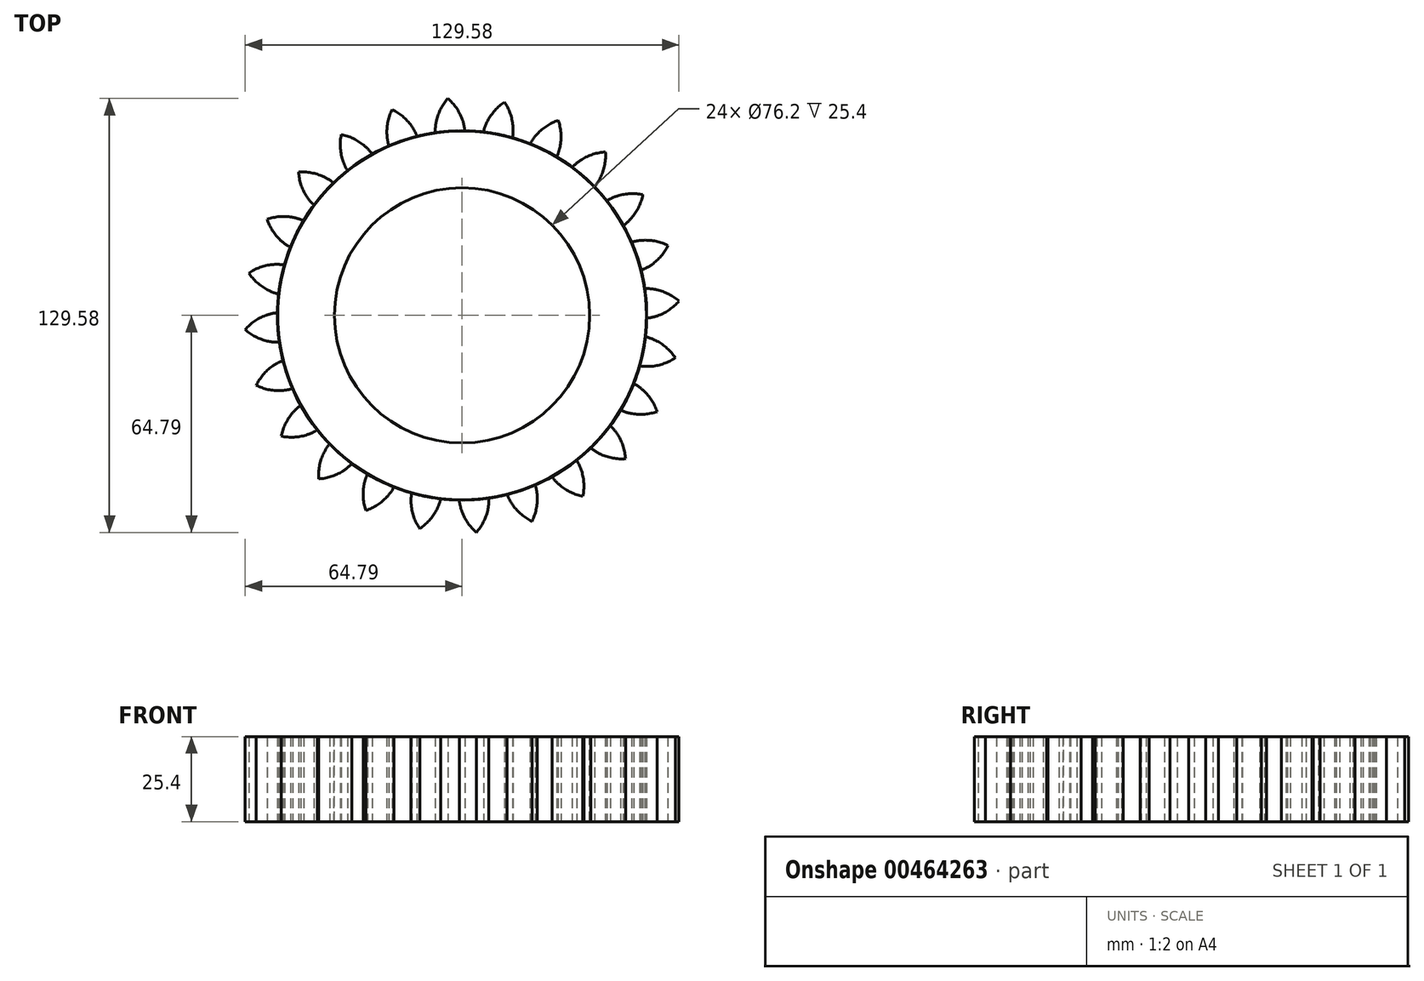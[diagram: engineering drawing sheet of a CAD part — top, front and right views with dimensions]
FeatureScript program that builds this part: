
annotation { "Feature Type Name" : "Feature", "Feature Type Description" : "" }
export const myFeature = defineFeature(function(context is Context, id is Id, definition is map)
    precondition{}
    {
        {
            var Q0;
            Q0=qCreatedBy(makeId("Top.planeOp"),FACE);
            var sketch = newSketch(context, id + "F0", { "sketchPlane" : qUnion([Q0])});
            skCircle(sketch, "E0", {"center": v(0, 0) * mm, "radius": 63.5 * mm, "construction": true});
            skCircle(sketch, "E1", {"center": v(0, 0) * mm, "radius": 58.67 * mm, "construction": true});
            skCircle(sketch, "E2", {"center": v(0, 0) * mm, "radius": 53.72 * mm});
            skLineSegment(sketch, "E3", {"start": v(0, 0) * mm, "end": v(0, 149.1) * mm, "construction": true});
            skLineSegment(sketch, "E4", {"start": v(0, 0) * mm, "end": v(-9.77, 149.1) * mm, "construction": true});
            skLineSegment(sketch, "E5", {"start": v(0, 58.67) * mm, "end": v(-102.58, 58.67) * mm, "construction": true});
            skLineSegment(sketch, "E6", {"start": v(0, 58.67) * mm, "end": v(-102.58, 21.34) * mm, "construction": true});
            skCircle(sketch, "E7", {"center": v(0, 0) * mm, "radius": 55.14 * mm});
            skCircle(sketch, "E8", {"center": v(0, 58.67) * mm, "radius": 14.6 * mm, "construction": true});
            skCircle(sketch, "E9", {"center": v(-13.72, 53.68) * mm, "radius": 14.6 * mm, "construction": true});
            skArc(sketch, "E10", {"start": v(0, 58.67) * mm, "mid": v(-1.74, 62) * mm, "end": v(-4.25, 64.8) * mm});
            skArc(sketch, "E11", {"start": v(0.88, 53.71) * mm, "mid": v(0.67, 56.23) * mm, "end": v(0, 58.67) * mm});
            skArc(sketch, "E12.MirrorCS", {"start": v(-7.66, 58.17) * mm, "mid": v(-6.37, 61.7) * mm, "end": v(-4.25, 64.8) * mm});
            skArc(sketch, "E13.MirrorCS", {"start": v(-7.88, 53.14) * mm, "mid": v(-8, 55.67) * mm, "end": v(-7.66, 58.17) * mm});
            skCircle(sketch, "E14", {"center": v(0, 0) * mm, "radius": 6.35 * mm});
            skSolve(sketch);
        }
        {
            var Q0;
            {var subQ0=sQuery(id+"F0.wireOp",EDGE,"E2");var subQ1=makeQuery(id+"F0.imprint","INTERSECT",VERTEX,{"derivedFrom":[subQ0,sQuery(id+"F0.wireOp",EDGE,"E11")]});Q0=makeQuery(id+"F0.imprint","IMPRINT",FACE,{"disambiguationData":[TD([[makeQuery(id+"F0.imprint","IMPRINT",EDGE,{"disambiguationData":[TD([[subQ1,-1.0]])],"derivedFrom":subQ0}),1.0]])]});}
            var Q1;
            {var subQ1=sQuery(id+"F0.wireOp",EDGE,"E10");Q1=makeQuery(id+"F0.imprint","IMPRINT",FACE,{"disambiguationData":[TD([[makeQuery(id+"F0.imprint","IMPRINT",EDGE,{"derivedFrom":subQ1}),1.0]])]});}
            var Q2;
            {var subQ0=sQuery(id+"F0.wireOp",EDGE,"E11");var subQ1=sQuery(id+"F0.wireOp",EDGE,"E2");var subQ2=makeQuery(id+"F0.imprint","INTERSECT",VERTEX,{"derivedFrom":[subQ1,subQ0]});Q2=makeQuery(id+"F0.imprint","IMPRINT",FACE,{"disambiguationData":[TD([[makeQuery(id+"F0.imprint","IMPRINT",EDGE,{"disambiguationData":[TD([[subQ2,-1.0]])],"derivedFrom":subQ1}),-1.0]])]});}
            var Q3;
            {var subQ0=sQuery(id+"F0.wireOp",EDGE,"E11");var subQ1=sQuery(id+"F0.wireOp",EDGE,"E2");var subQ2=makeQuery(id+"F0.imprint","INTERSECT",VERTEX,{"derivedFrom":[subQ1,subQ0]});Q3=makeQuery(id+"F0.imprint","IMPRINT",FACE,{"disambiguationData":[TD([[makeQuery(id+"F0.imprint","IMPRINT",EDGE,{"disambiguationData":[TD([[subQ2,1.0]])],"derivedFrom":subQ1}),-1.0]])]});}
            extrude(context, id + "F1", {"entities" : qUnion([Q0, Q1, Q2, Q3]), "depth" : 25.4 * mm});
        }
        {
            var Q0;
            Q0=makeQuery(id+"F1.opExtrude","SWEPT_BODY",BODY,{"disambiguationData":[OSD([sQuery(id+"F0.wireOp",EDGE,"E7"),sQuery(id+"F0.wireOp",EDGE,"E10"),sQuery(id+"F0.wireOp",EDGE,"E11"),sQuery(id+"F0.wireOp",EDGE,"E12.MirrorCS"),sQuery(id+"F0.wireOp",EDGE,"E13.MirrorCS")])]});
            var Q1;
            Q1=makeQuery(id+"F1.opExtrude","SWEPT_FACE",FACE,{"disambiguationData":[OSD([sQuery(id+"F0.wireOp",EDGE,"E7")])]});
            circularPattern(context, id + "F2", {"entities" : qUnion([Q0]), "axis" : qUnion([Q1]), "angle" : 360 * degree, "instanceCount" : 24, "equalSpace" : true});
        }
        {
            var Q0;
            Q0=makeQuery(id+"F1.opExtrude","CAP_FACE",FACE,{"disambiguationData":[OSD([sQuery(id+"F0.wireOp",EDGE,"E7"),sQuery(id+"F0.wireOp",EDGE,"E10"),sQuery(id+"F0.wireOp",EDGE,"E11"),sQuery(id+"F0.wireOp",EDGE,"E12.MirrorCS"),sQuery(id+"F0.wireOp",EDGE,"E13.MirrorCS")])],"isStart":false});
            var sketch = newSketch(context, id + "F3", { "sketchPlane" : qUnion([Q0])});
            skCircle(sketch, "E15", {"center": v(0, 0) * mm, "radius": 38.1 * mm});
            skSolve(sketch);
        }
        {
            var Q0;
            Q0=makeQuery(id+"F3.imprint","IMPRINT",FACE,{"disambiguationData":[TD([[makeQuery(id+"F3.imprint","IMPRINT",EDGE,{"derivedFrom":sQuery(id+"F3.wireOp",EDGE,"E15")}),1.0]])]});
            var Q1;
            Q1=sQuery(id+"F3.wireOp",EDGE,"E15");
            extrude(context, id + "F4", {"entities" : qUnion([Q0]), "operationType" : NewBodyOperationType.REMOVE, "surfaceEntities" : qUnion([Q1]), "oppositeDirection" : true, "depth" : 25.4 * mm});
        }
        {
            var Q0;
            Q0=makeQuery(id+"F2.opPattern","COPY",FACE,{"derivedFrom":makeQuery(id+"F1.opExtrude","CAP_FACE",FACE,{"disambiguationData":[OSD([sQuery(id+"F0.wireOp",EDGE,"E7"),sQuery(id+"F0.wireOp",EDGE,"E10"),sQuery(id+"F0.wireOp",EDGE,"E11"),sQuery(id+"F0.wireOp",EDGE,"E12.MirrorCS"),sQuery(id+"F0.wireOp",EDGE,"E13.MirrorCS")])],"isStart":false}),"instanceName":"12"});
            var sketch = newSketch(context, id + "F5", { "sketchPlane" : qUnion([Q0])});
            skCircle(sketch, "E16", {"center": v(0, 0) * mm, "radius": 6.35 * mm});
            skSolve(sketch);
        }
        {
            var Q0;
            Q0=makeQuery(id+"F5.imprint","IMPRINT",FACE,{"disambiguationData":[TD([[makeQuery(id+"F5.imprint","IMPRINT",EDGE,{"derivedFrom":sQuery(id+"F5.wireOp",EDGE,"E16")}),1.0]])]});
            extrude(context, id + "F6", {"entities" : qUnion([Q0]), "operationType" : NewBodyOperationType.REMOVE, "oppositeDirection" : true, "depth" : 25.4 * mm});
        }
    });
